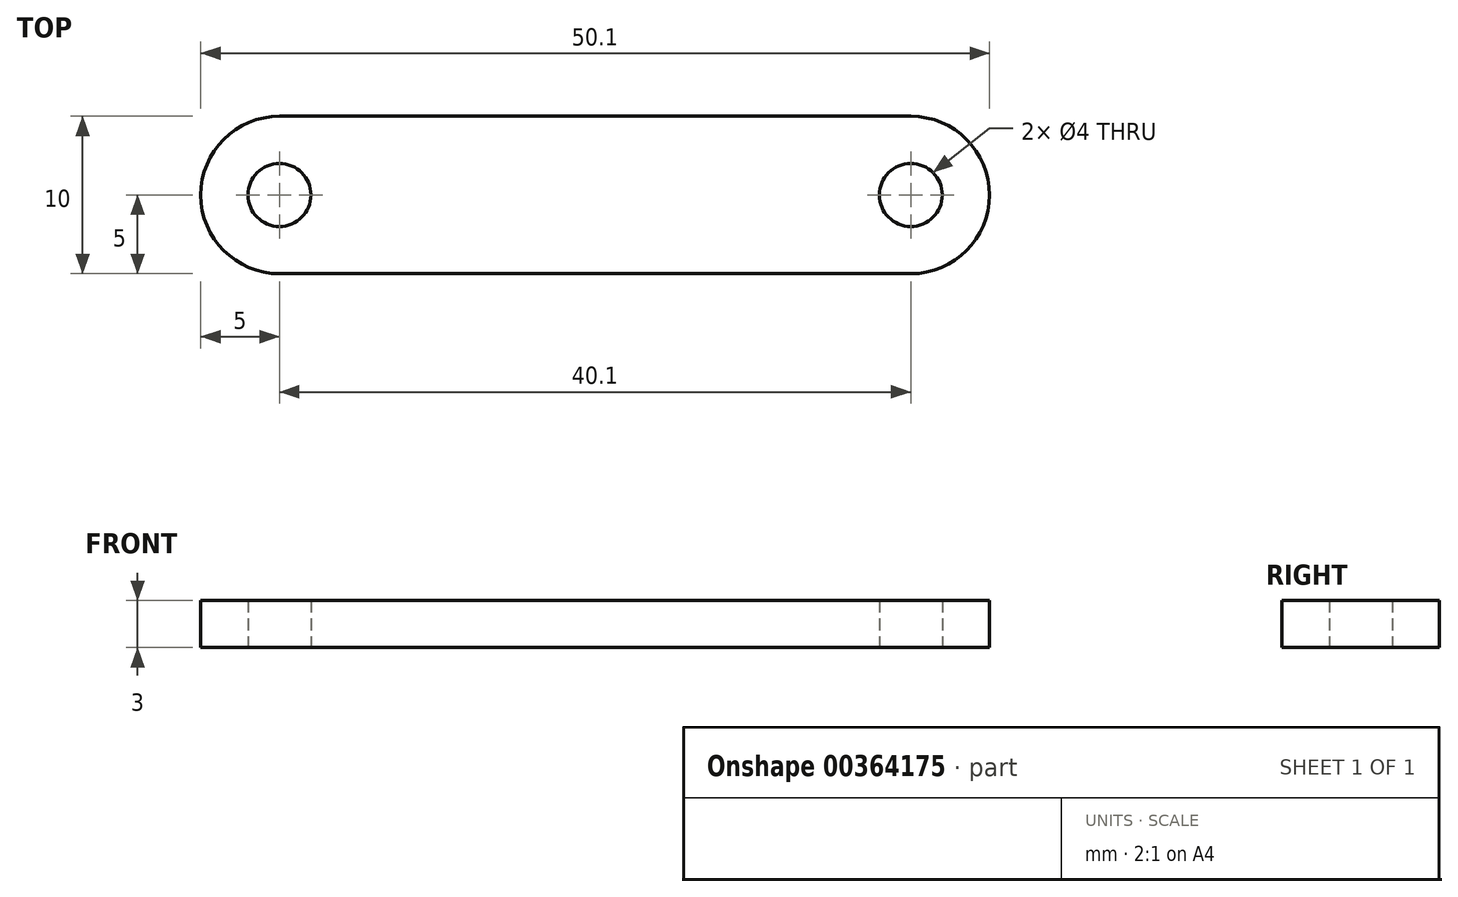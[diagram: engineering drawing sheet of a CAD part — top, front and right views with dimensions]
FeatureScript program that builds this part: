
annotation { "Feature Type Name" : "Feature", "Feature Type Description" : "" }
export const myFeature = defineFeature(function(context is Context, id is Id, definition is map)
    precondition{}
    {
        {
            var Q0;
            Q0=qCreatedBy(makeId("Top.planeOp"),FACE);
            var sketch = newSketch(context, id + "F0", { "sketchPlane" : qUnion([Q0])});
            skLineSegment(sketch, "E0.bottom", {"start": v(20.05, 5) * mm, "end": v(-20.05, 5) * mm});
            skLineSegment(sketch, "E0.top", {"start": v(20.05, -5) * mm, "end": v(-20.05, -5) * mm});
            skPoint(sketch, "E0.middle", {"position": v(0, 0) * mm});
            skCircle(sketch, "E1", {"center": v(-20.05, 0) * mm, "radius": 2 * mm});
            skCircle(sketch, "E2", {"center": v(20.05, 0) * mm, "radius": 2 * mm});
            skArc(sketch, "E3", {"start": v(-20.05, 5) * mm, "mid": v(-25.05, 0) * mm, "end": v(-20.05, -5) * mm});
            skArc(sketch, "E4", {"start": v(20.05, -5) * mm, "mid": v(25.05, 0) * mm, "end": v(20.05, 5) * mm});
            skSolve(sketch);
        }
        {
            var Q0;
            Q0=qSketchRegion(id+"F0",true);
            extrude(context, id + "F1", {"entities" : qUnion([Q0]), "depth" : 3 * mm});
        }
    });
